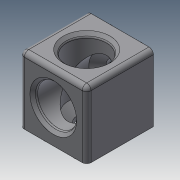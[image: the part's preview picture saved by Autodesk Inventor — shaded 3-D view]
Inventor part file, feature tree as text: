
AUTODESK INVENTOR PART (.ipt)
format: ipt  version: 2018.3 (Build 223284000, 284)  size: 265,728 bytes
history: native  units: in
note: dims shown in document units (in); Inventor stores cm internally (conversion verified against a paired STEP export)
features: fillet x1, revolve x1, mirror x1
ambient origin geometry x8: Origin, YZ Plane, XZ Plane, XY Plane, X Axis, Y Axis, Z Axis, Center Point
bodies: Solid1 (feature_tree), Solid2 (feature_tree), Solid3 (feature_tree)
feature tree (3):
  fillet  "Fillet2"  [1 undecoded]
  revolve  "Revolve1"  [1 undecoded]
  mirror  "Mirror2"
note: 2 required parameter values undecoded (feature->parameter linkage not recoverable at this tier; creation-order binding heuristic only, values carry confidence <= 0.55)
